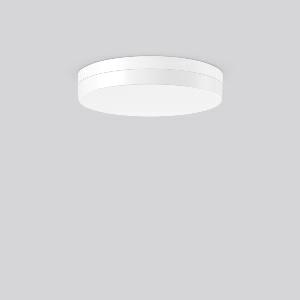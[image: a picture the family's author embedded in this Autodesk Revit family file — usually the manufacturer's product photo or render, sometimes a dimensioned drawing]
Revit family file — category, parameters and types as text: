
# Revit family: flat_slim_round_312631_002_76_06f9
name_source: partatom
category: Lighting Fixtures
units: mm (PartAtom-declared; Revit-internal decimal feet)

## family parameters
Cut with Voids When Loaded = No
Host = Face
Light Source = No
Part Type = Normal
Room Calculation Point = No
Round Connector Dimension = Use Diameter
Shared = No

## types (1)
- MultiLumen 1 830 (1 x LED Modul 830, 2450 lm, 3000)
    Apparent Load = 25 VA
    CIE Flux Codes = 40 70 90 84 100
    Color Rendering = 80
    Color Temperature = 3000
    Default Elevation = 1800 mm
    Height = 75 mm
    Lamp = 1 x LED Modul 830
    Lamp Light Flux = 2450 lm
    Lamp count = 1
    Length = 400 mm
    Lifetime = 50000 h
    Luminous efficacy = 98 lm/W
    Manufacturer = RZB
    ModVariant = No
    Model = 312631.002.76
    Mounting Place = Ceiling
    Mounting Type = Surface mounted
    Number of Poles = 1
    OnlyDefault = Yes
    Power Factor = 1
    Product Name = FLAT SLIM round
    Product group = Surface mounted ceiling and wall luminaires
    ProductGroupID = 305
    Protection Class = Protection class I
    Protection Degree = Degree of protection
    RLX_Detail_Level = 1
    RLX_Emergency_Light_Flux = 0 lm
    RLX_Emergency_Type = 0
    RLX_Emergency_Type_DB = No
    RlxData = <blob elided: 20053 chars, md5=3e78956f>
    Socket = socket
    Standby Power = 0 W
    System Light Flux = 2450 lm
    System Power = 25 W
    Type Comments = MultiLumen 1 830
    Type Image = 312631.002.jpg
    URL = http://relux.com
    VarID = multilumen_1_830
    Voltage = 0 V
    Weight = 0.00 kg
    Width = 0 mm  [stored 0 ft]

note: [stored X ft] marks values corroborated as IEEE doubles in the binary element streams (Revit-internal decimal feet)

## geometry (parser evidence)
native form markers: Blend x4, Sweep x14
no freeform markers — native parametric forms only
